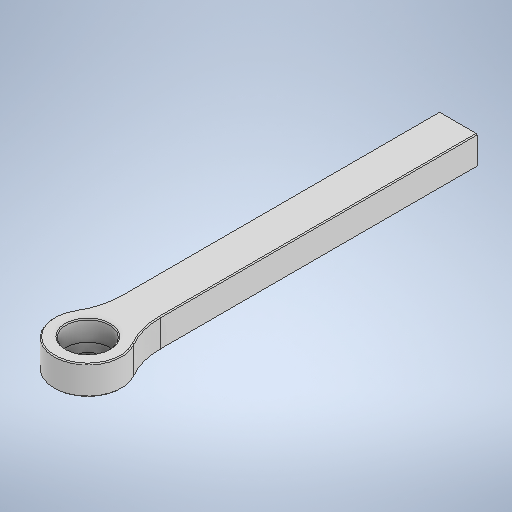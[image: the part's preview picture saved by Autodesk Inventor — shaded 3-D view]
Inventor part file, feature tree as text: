
AUTODESK INVENTOR PART (.ipt)
format: ipt  version: 2025.1 (Build 291241000, 241)  size: 306,688 bytes
history: native  units: mm
features: extrude x4, sketch x4, fillet x3
ambient origin geometry x8: Origin, YZ Plane, XZ Plane, XY Plane, X Axis, Y Axis, Z Axis, Center Point
bodies: Body1 (feature_tree)
feature tree (11):
  extrude  "Extrusion1"  TaperAngle=0.0deg  [1 undecoded]
  extrude  "Extrusion2"  Depth=6.0mm TaperAngle=0.0deg
  fillet  "Rundung1"  Radius=4.0mm
  fillet  "Rundung2"  Radius=4.0mm
  extrude  "Extrusion3"  Depth=4.2mm TaperAngle=0.0deg
  fillet  "Rundung3"  Radius=0.2mm
  extrude  "Extrusion4"  Depth=4.0mm
  sketch  "Skizze1"  dims[d1=14.0mm d3=15.0mm d4=15.0mm d7=0.0mm d8=77.0mm d9=0.0mm]
  sketch  "Skizze4"  dims[d10=0.0mm d11=6.0mm d12=0.0mm d20=4.0mm d21=4.0mm]
  sketch  "Skizze5"  dims[d22=9.0mm d23=4.2mm d24=0.0mm d25=0.2mm]
  sketch  "Skizze6"  dims[d26=0.2mm d27=3.5mm d28=4.2mm d29=0.0mm d30=0.2mm d31=3.5mm d32=3.0mm d33=4.0mm d34=4.0mm d35=0.0mm]
note: 1 required parameter value undecoded (feature->parameter linkage not recoverable at this tier; creation-order binding heuristic only, values carry confidence <= 0.55)
